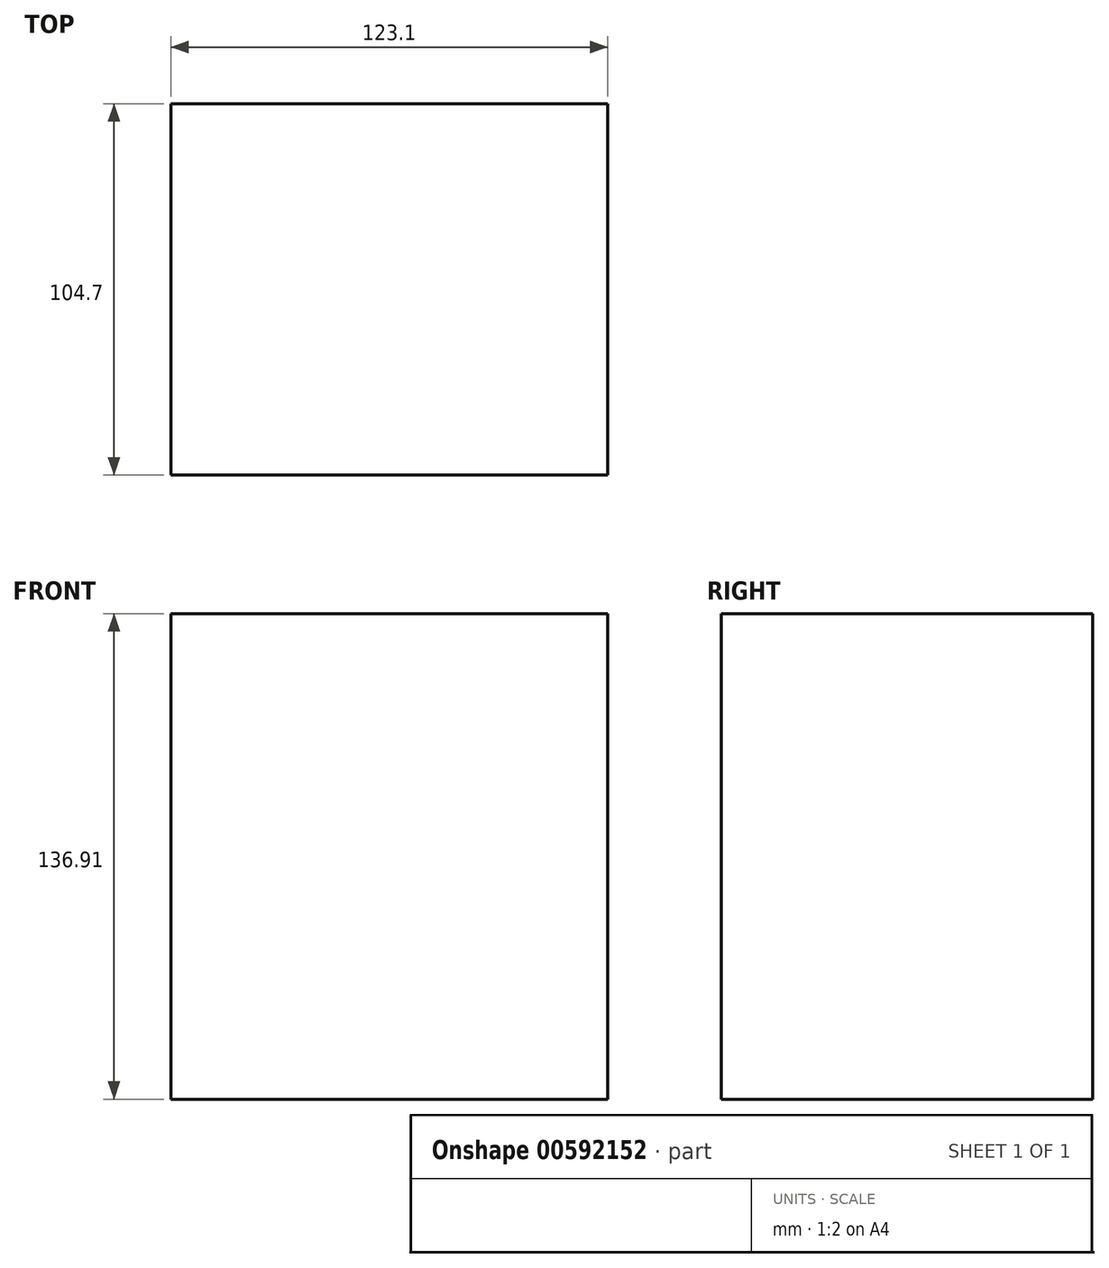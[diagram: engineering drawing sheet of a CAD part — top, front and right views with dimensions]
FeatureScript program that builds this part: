
annotation { "Feature Type Name" : "Feature", "Feature Type Description" : "" }
export const myFeature = defineFeature(function(context is Context, id is Id, definition is map)
    precondition{}
    {
        {
            var Q0;
            Q0=qCreatedBy(makeId("Top.planeOp"),FACE);
            var sketch = newSketch(context, id + "F0", { "sketchPlane" : qUnion([Q0])});
            skLineSegment(sketch, "E0.bottom", {"start": v(61.55, 52.35) * mm, "end": v(-61.55, 52.35) * mm});
            skLineSegment(sketch, "E0.top", {"start": v(61.55, -52.35) * mm, "end": v(-61.55, -52.35) * mm});
            skLineSegment(sketch, "E0.left", {"start": v(61.55, 52.35) * mm, "end": v(61.55, -52.35) * mm});
            skLineSegment(sketch, "E0.right", {"start": v(-61.55, 52.35) * mm, "end": v(-61.55, -52.35) * mm});
            skPoint(sketch, "E0.middle", {"position": v(0, 0) * mm});
            skSolve(sketch);
        }
        {
            var Q0;
            Q0=makeQuery(id+"F0.imprint","IMPRINT",FACE,{"disambiguationData":[TD([[makeQuery(id+"F0.imprint","IMPRINT",EDGE,{"derivedFrom":sQuery(id+"F0.wireOp",EDGE,"E0.bottom")}),1.0]])]});
            extrude(context, id + "F1", {"entities" : qUnion([Q0]), "depth" : 136.9 * mm, "offsetDistance" : 25.4 * mm});
        }
    });
